# Revit family: AV-01
name_source: partatom
category: Устройства связи
revit_build: Autodesk Revit 2016 (Build: 20160314_0715(x64)
units: mm (PartAtom-declared; Revit-internal decimal feet)

## family parameters
Всегда вертикально = Нет
На основе рабочей плоскости = Да
Общий = Да
При загрузке вырезать с полостями = Нет
Размер круглого соединителя = Использовать диаметр
Сохранять ориентацию аннотаций = Нет
Тип детали = Нормальный
Точка расчета площади = Нет

## types (3) — shared parameters
ADSK_URL документации изделия = https://wiki.bas-ip.com
ADSK_Версия Revit = Revit 2016
ADSK_Единица измерения = шт
ADSK_Завод-изготовитель = BAS-IP
ADSK_Классификация нагрузок = Вызывная панель
ADSK_Количество фаз = 1
ADSK_Коэффициент мощности = 0.9
ADSK_Напряжение = 12 В
ADSK_Номинальная мощность = 6 Вт
ADSK_Полная мощность = 6 В·А
ADSK_Размер_Длина = 115 мм
ADSK_Размер_Толщина = 45 мм
ADSK_Размер_Ширина = 190 мм
BIM library = https://bimlib.ru
URL = https://www.bas-ip.ru
Аутентификация = Отдельный пароль на настройки, WEB–интерфейс
Выходное видео = D1 (704×576), H.264 Main Profile, BaseLine Profile
Группа модели = Вызывная панель
Дисплей = Нет
Изготовитель = BAS-IP
Изображение типоразмера = <Нет>
Интеграция со СКУД = Нет
Интерфейс = WEB-интерфейс
Камера = 1/3”, регулировка направления камеры
Класс степени защиты = IP65
Кнопки быстрого вызова = 1 сенсорная кнопка вызова
Количество мелодий вызова = 4 полифонические мелодии
Корпус = Металлический
Материал корпуса = SHV_Титан
Минимальная освещенность = 0,01 LuX
Ночная подсветка = 6 светодиодов
Питание = + 12 В
Потребление питания = 5,5 Вт, в режиме ожидания – 2,5 Вт
Размер под установку = 94х151х45 мм
Размер самой панели = 99х159х48мм
Разрешение камеры = 800 ТВл
Режим разговора = Двухсторонний
Температурный режим = -40 ... +65 °С
Тип клавиатуры = Нет
Тип панели = Индивидуальная
Тип установки = Врезная, накладная с BR-AV2
Угол обзора = По горизонтали 78°, по вертикали 56°
Цветовое решение = Титаново-серый
zero-valued in all types: Отметка по умолчанию

## per-type parameters (varying)
| type | ADSK_URL страницы изделия | ADSK_Наименование | Дополнительно | Изображение | Контроль доступа | Описание | Открытие замка |
| AV-01 | https://www.bas-ip.ru
https://wiki.bas-ip.com | ВЫЗЫВНАЯ ПАНЕЛЬ AV-01 | SIP P2P; Место для подписи возле кнопки вызова | SHV_Изображение_AV-01 | Нет | Данная индивидуальная вызывная панель сильно отличается в лучшую сторону по дизайну и характеристикам от обычных панелей, установленных в домах и квартирах. Благодаря степени защиты IP-65, панель можно без проблем устанавливать на улице, не боясь сильного дождя и прочих “радостей” природы. | С монитора |
| AV-01T | https://www.bas-ip.ru
https://wiki.bas-ip.com | ВЫЗЫВНАЯ ПАНЕЛЬ AV-01T | SIP P2P; Место для подписи возле кнопки вызова | SHV_Изображение_AV-01T | Считыватель беcконтактных карт EM-Marin (AV-01TE), считыватель беcконтактных карт Mifare (AV-01TM) | Данная индивидуальная вызывная панель сильно отличается в лучшую сторону по дизайну и характеристикам от обычных панелей, установленных в домах и квартирах. Благодаря степени защиты IP-65, панель можно без проблем устанавливать на улице, не боясь сильного дождя и прочих “радостей” природы. | С монитора, по карте |
| AV-01K | https://www.bas-ip.ru | ВЫЗЫВНАЯ ПАНЕЛЬ AV-01K | SIP P2P; Место для подписи возле кнопки вызова, работа в двух режимах: индивидуальный и многоабонентский | SHV_Изображение_AV-01K | Разблокировка замка с помощью кода | AV-01K - это индивидуальная вызывная панель с кодовым набором. Данная панель может работать в двух режимах – индивидуальном и многоабонентском. В индивидуальном режиме клавиатура панели служит кодонаборной панелью для открытия замка, а с помощью кнопки прямого вызова можно связаться с нужным монитором. | С монитора, по коду |

note: column(s) folded — value = type name in every type: ADSK_Марка, ADSK_Наименование краткое
